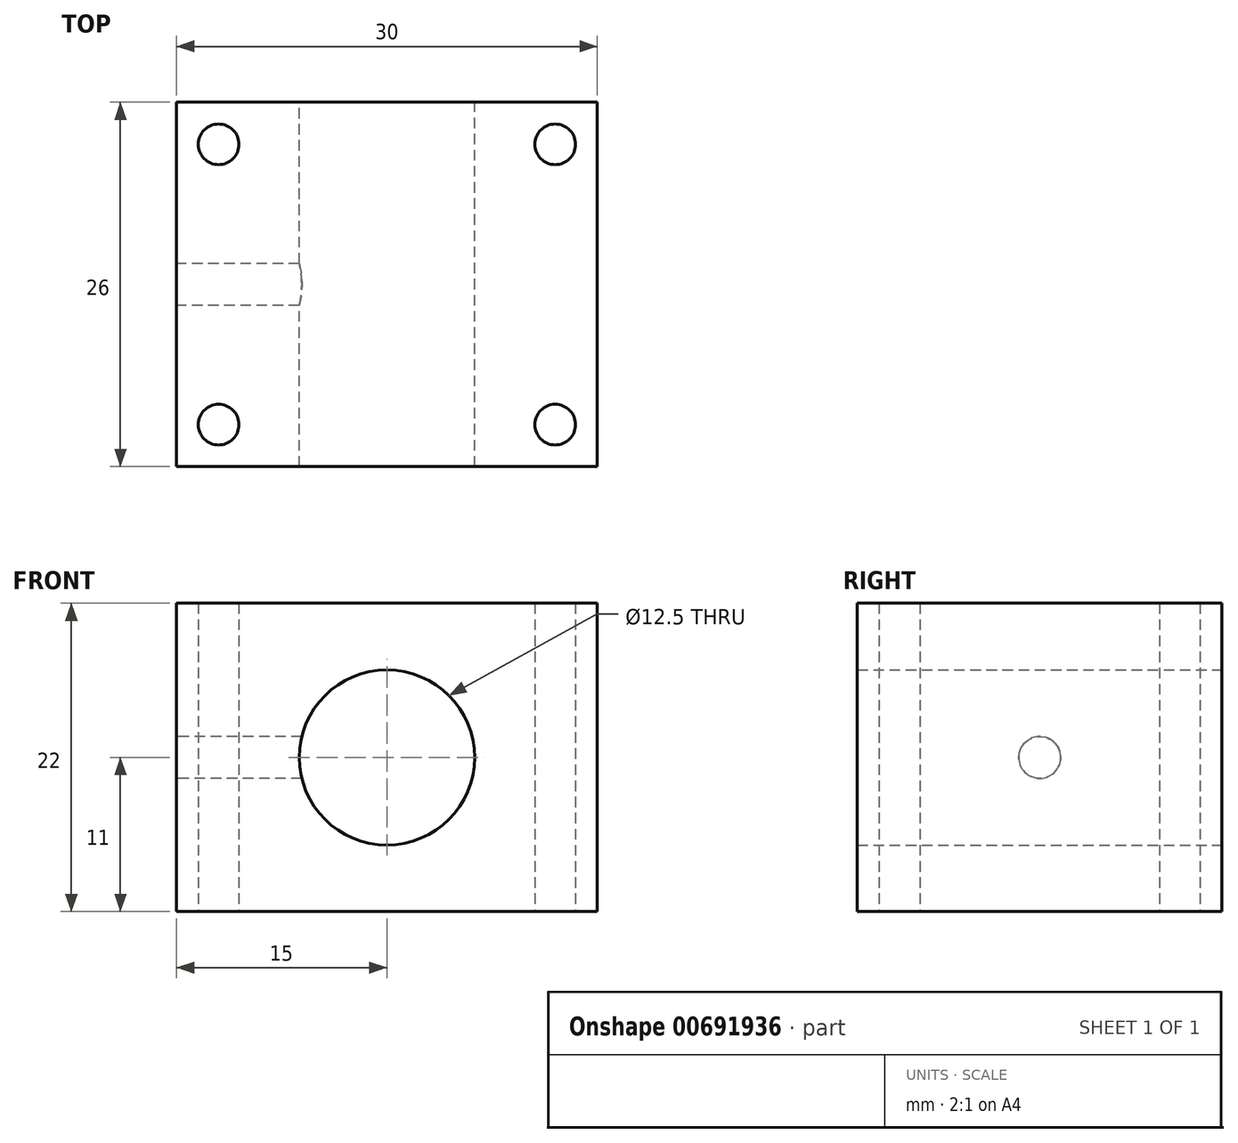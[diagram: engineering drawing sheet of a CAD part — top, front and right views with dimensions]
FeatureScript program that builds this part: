
annotation { "Feature Type Name" : "Feature", "Feature Type Description" : "" }
export const myFeature = defineFeature(function(context is Context, id is Id, definition is map)
    precondition{}
    {
        {
            var Q0;
            Q0=qCreatedBy(makeId("Top.planeOp"),FACE);
            var sketch = newSketch(context, id + "F0", { "sketchPlane" : qUnion([Q0])});
            skLineSegment(sketch, "E0.bottom", {"start": v(15, -13) * mm, "end": v(-15, -13) * mm});
            skLineSegment(sketch, "E0.top", {"start": v(15, 13) * mm, "end": v(-15, 13) * mm});
            skLineSegment(sketch, "E0.left", {"start": v(15, -13) * mm, "end": v(15, 13) * mm});
            skLineSegment(sketch, "E0.right", {"start": v(-15, -13) * mm, "end": v(-15, 13) * mm});
            skPoint(sketch, "E0.middle", {"position": v(0, 0) * mm});
            skCircle(sketch, "E1", {"center": v(-12, 10) * mm, "radius": 1.45 * mm});
            skCircle(sketch, "E2.MirrorC", {"center": v(12, 10) * mm, "radius": 1.45 * mm});
            skCircle(sketch, "E3.MirrorC", {"center": v(-12, -10) * mm, "radius": 1.45 * mm});
            skCircle(sketch, "E4.MirrorC", {"center": v(12, -10) * mm, "radius": 1.45 * mm});
            skSolve(sketch);
        }
        {
            var Q0;
            Q0=makeQuery(id+"F0.imprint","IMPRINT",FACE,{"disambiguationData":[TD([[makeQuery(id+"F0.imprint","IMPRINT",EDGE,{"derivedFrom":sQuery(id+"F0.wireOp",EDGE,"E0.bottom")}),-1.0]])]});
            extrude(context, id + "F1", {"entities" : qUnion([Q0]), "depth" : 22 * mm, "offsetDistance" : 25 * mm});
        }
        {
            var Q0;
            Q0=makeQuery(id+"F1.opExtrude","SWEPT_FACE",FACE,{"disambiguationData":[OSD([sQuery(id+"F0.wireOp",EDGE,"E0.top")])]});
            var sketch = newSketch(context, id + "F2", { "sketchPlane" : qUnion([Q0])});
            skLineSegment(sketch, "E5.0", {"start": v(15, 22) * mm, "end": v(15, 0) * mm});
            skLineSegment(sketch, "E6.0", {"start": v(-15, 22) * mm, "end": v(15, 22) * mm});
            skLineSegment(sketch, "E7.0", {"start": v(-15, 22) * mm, "end": v(-15, 0) * mm});
            skLineSegment(sketch, "E8", {"start": v(15, 11) * mm, "end": v(-15, 11) * mm, "construction": true});
            skCircle(sketch, "E9", {"center": v(0, 11) * mm, "radius": 6.25 * mm});
            skSolve(sketch);
        }
        {
            var Q0;
            {var subQ0=sQuery(id+"F2.wireOp",EDGE,"kRw48zZT-po2z-dxeW-f22o-9pQk8CH6DV85.top");var subQ1=sQuery(id+"F2.wireOp",EDGE,"E9");var subQ2=makeQuery(id+"F2.imprint","INTERSECT",VERTEX,{"disambiguationData":[OD(0.0)],"derivedFrom":[subQ1,subQ0]});Q0=makeQuery(id+"F2.imprint","IMPRINT",FACE,{"disambiguationData":[TD([[makeQuery(id+"F2.imprint","IMPRINT",EDGE,{"disambiguationData":[TD([[subQ2,-1.0]])],"derivedFrom":subQ1}),1.0]])]});}
            var Q1;
            {var subQ0=sQuery(id+"F2.wireOp",EDGE,"kRw48zZT-po2z-dxeW-f22o-9pQk8CH6DV85.bottom");var subQ1=sQuery(id+"F2.wireOp",EDGE,"E9");var subQ2=makeQuery(id+"F2.imprint","INTERSECT",VERTEX,{"disambiguationData":[OD(0.0)],"derivedFrom":[subQ1,subQ0]});Q1=makeQuery(id+"F2.imprint","IMPRINT",FACE,{"disambiguationData":[TD([[makeQuery(id+"F2.imprint","IMPRINT",EDGE,{"disambiguationData":[TD([[subQ2,-1.0]])],"derivedFrom":subQ1}),1.0]])]});}
            var Q2;
            {var subQ0=sQuery(id+"F2.wireOp",EDGE,"kRw48zZT-po2z-dxeW-f22o-9pQk8CH6DV85.bottom");var subQ1=sQuery(id+"F2.wireOp",EDGE,"E9");var subQ2=makeQuery(id+"F2.imprint","INTERSECT",VERTEX,{"disambiguationData":[OD(0.0)],"derivedFrom":[subQ1,subQ0]});Q2=makeQuery(id+"F2.imprint","IMPRINT",FACE,{"disambiguationData":[TD([[makeQuery(id+"F2.imprint","IMPRINT",EDGE,{"disambiguationData":[TD([[subQ2,1.0]])],"derivedFrom":subQ1}),1.0]])]});}
            var Q3;
            Q3=makeQuery(id+"F2.imprint","IMPRINT",FACE,{"disambiguationData":[TD([[makeQuery(id+"F2.imprint","IMPRINT",EDGE,{"derivedFrom":sQuery(id+"F2.wireOp",EDGE,"E9")}),1.0]])]});
            extrude(context, id + "F3", {"entities" : qUnion([Q0, Q1, Q2, Q3]), "operationType" : NewBodyOperationType.REMOVE, "endBound" : BoundingType.THROUGH_ALL, "oppositeDirection" : true, "depth" : 25 * mm, "offsetDistance" : 25 * mm});
        }
        {
            var Q0;
            Q0=makeQuery(id+"F1.opExtrude","SWEPT_FACE",FACE,{"disambiguationData":[OSD([sQuery(id+"F0.wireOp",EDGE,"E0.right")])]});
            var sketch = newSketch(context, id + "F4", { "sketchPlane" : qUnion([Q0])});
            skCircle(sketch, "E10", {"center": v(0, 11) * mm, "radius": 1.5 * mm});
            skLineSegment(sketch, "E11", {"start": v(0, 0) * mm, "end": v(0, 22) * mm, "construction": true});
            skSolve(sketch);
        }
        {
            var Q0;
            Q0 = qSketchRegion(id + "F4", true);
            extrude(context, id + "F5", {"entities" : qUnion([Q0]), "operationType" : NewBodyOperationType.REMOVE, "oppositeDirection" : true, "depth" : 13 * mm, "offsetDistance" : 25 * mm});
        }
    });
